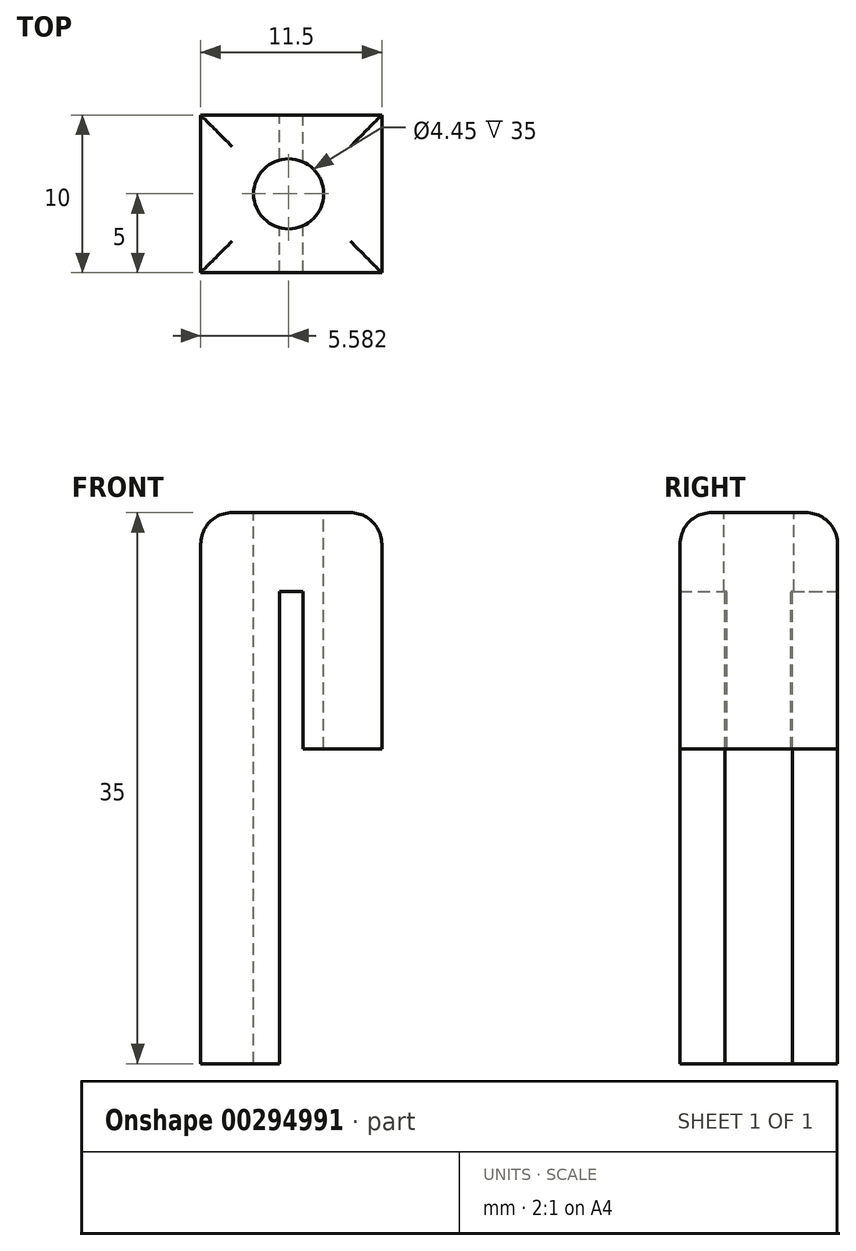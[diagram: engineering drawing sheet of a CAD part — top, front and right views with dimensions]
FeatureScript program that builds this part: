
annotation { "Feature Type Name" : "Feature", "Feature Type Description" : "" }
export const myFeature = defineFeature(function(context is Context, id is Id, definition is map)
    precondition{}
    {
        {
            var Q0;
            Q0=qCreatedBy(makeId("Front.planeOp"),FACE);
            var sketch = newSketch(context, id + "F0", { "sketchPlane" : qUnion([Q0])});
            skLineSegment(sketch, "E0", {"start": v(53.2, 39.36) * mm, "end": v(53.2, 9.36) * mm});
            skLineSegment(sketch, "E1", {"start": v(53.2, 9.36) * mm, "end": v(48.2, 9.36) * mm});
            skLineSegment(sketch, "E2", {"start": v(48.2, 9.36) * mm, "end": v(48.2, 44.36) * mm});
            skLineSegment(sketch, "E3", {"start": v(48.2, 44.36) * mm, "end": v(59.7, 44.36) * mm});
            skLineSegment(sketch, "E4", {"start": v(59.7, 44.36) * mm, "end": v(59.7, 29.36) * mm});
            skLineSegment(sketch, "E5", {"start": v(59.7, 29.36) * mm, "end": v(54.7, 29.36) * mm});
            skLineSegment(sketch, "E6", {"start": v(54.7, 29.36) * mm, "end": v(54.7, 39.36) * mm});
            skLineSegment(sketch, "E7", {"start": v(54.7, 39.36) * mm, "end": v(53.2, 39.36) * mm});
            skSolve(sketch);
        }
        {
            var Q0;
            Q0=makeQuery(id+"F0.imprint","IMPRINT",FACE,{"disambiguationData":[TD([[makeQuery(id+"F0.imprint","IMPRINT",EDGE,{"derivedFrom":sQuery(id+"F0.wireOp",EDGE,"E0")}),-1.0]])]});
            extrude(context, id + "F1", {"entities" : qUnion([Q0]), "endBound" : BoundingType.SYMMETRIC, "depth" : 10 * mm});
        }
        {
            var Q0;
            Q0=makeQuery(id+"F1.opExtrude","SWEPT_EDGE",EDGE,{"disambiguationData":[OSD([sQuery(id+"F0.wireOp",EDGE,"E3"),sQuery(id+"F0.wireOp",EDGE,"E4")])]});
            var Q1;
            Q1=makeQuery(id+"F1.opExtrude","CAP_EDGE",EDGE,{"disambiguationData":[OSD([sQuery(id+"F0.wireOp",EDGE,"E3")])],"isStart":true});
            var Q2;
            Q2=makeQuery(id+"F1.opExtrude","CAP_EDGE",EDGE,{"disambiguationData":[OSD([sQuery(id+"F0.wireOp",EDGE,"E3")])],"isStart":false});
            var Q3;
            Q3=makeQuery(id+"F1.opExtrude","SWEPT_EDGE",EDGE,{"disambiguationData":[OSD([sQuery(id+"F0.wireOp",EDGE,"E2"),sQuery(id+"F0.wireOp",EDGE,"E3")])]});
            fillet(context, id + "F2", {"entities" : qUnion([Q0, Q1, Q2, Q3]), "radius" : 2 * mm, "tangentPropagation" : true, "allowEdgeOverflow" : false});
        }
        {
            var Q0;
            Q0=makeQuery(id+"F1.opExtrude","SWEPT_FACE",FACE,{"disambiguationData":[OSD([sQuery(id+"F0.wireOp",EDGE,"E3")])]});
            var sketch = newSketch(context, id + "F3", { "sketchPlane" : qUnion([Q0])});
            skCircle(sketch, "E8", {"center": v(53.8, 0) * mm, "radius": 2.22 * mm});
            skSolve(sketch);
        }
        {
            var Q0;
            Q0=makeQuery(id+"F3.imprint","IMPRINT",FACE,{"disambiguationData":[TD([[makeQuery(id+"F3.imprint","IMPRINT",EDGE,{"derivedFrom":sQuery(id+"F3.wireOp",EDGE,"E8")}),1.0]])]});
            extrude(context, id + "F4", {"entities" : qUnion([Q0]), "operationType" : NewBodyOperationType.REMOVE, "endBound" : BoundingType.THROUGH_ALL, "oppositeDirection" : true, "depth" : 25 * mm});
        }
    });
